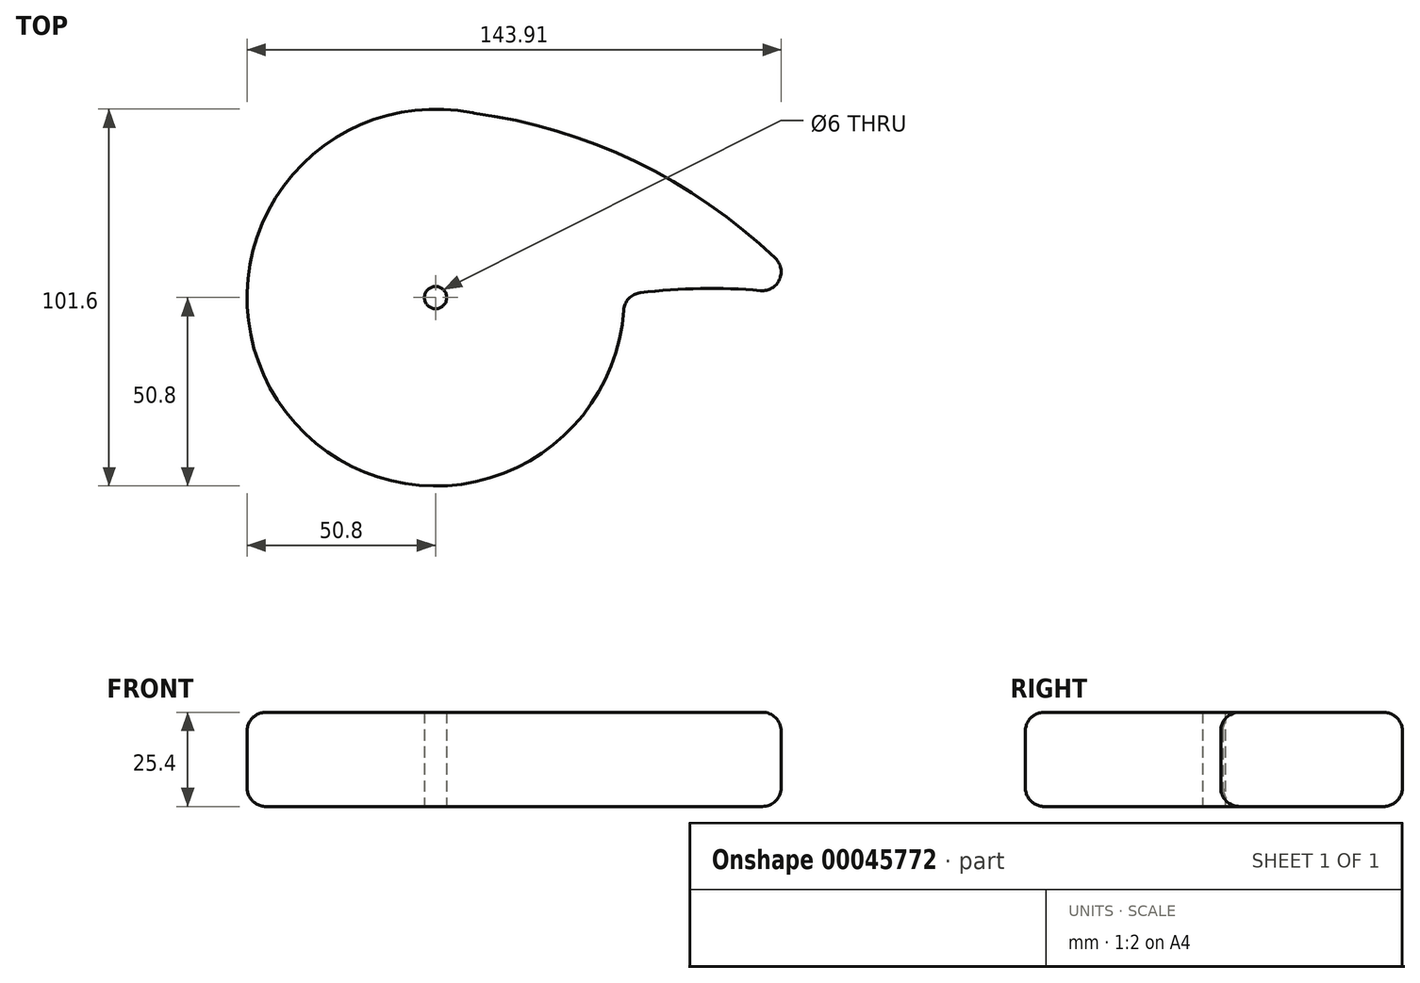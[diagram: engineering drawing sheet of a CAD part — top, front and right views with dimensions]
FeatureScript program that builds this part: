
annotation { "Feature Type Name" : "Feature", "Feature Type Description" : "" }
export const myFeature = defineFeature(function(context is Context, id is Id, definition is map)
    precondition{}
    {
        {
            var Q0;
            Q0=qCreatedBy(makeId("Top.planeOp"),FACE);
            var sketch = newSketch(context, id + "F0", { "sketchPlane" : qUnion([Q0])});
            skPoint(sketch, "E0", {"position": v(0, 50.8) * mm});
            skPoint(sketch, "E1", {"position": v(46.63, 0) * mm});
            skArc(sketch, "E2", {"start": v(10.1, 49.78) * mm, "mid": v(-39.11, -32.42) * mm, "end": v(50.8, 0.7) * mm});
            skPoint(sketch, "E3", {"position": v(0, 3) * mm});
            skCircle(sketch, "E4", {"center": v(0, 0) * mm, "radius": 3 * mm});
            skPoint(sketch, "E5", {"position": v(101.6, 0) * mm});
            skArc(sketch, "E6", {"start": v(101.6, 0) * mm, "mid": v(55.92, 35.65) * mm, "end": v(0, 50.8) * mm});
            skArc(sketch, "E7", {"start": v(101.6, 0) * mm, "mid": v(76.23, 2.45) * mm, "end": v(50.8, 0.7) * mm});
            skSolve(sketch);
        }
        {
            var Q0;
            Q0 = qSketchRegion(id + "F0", true);
            extrude(context, id + "F1", {"entities" : qUnion([Q0]), "depth" : 25.4 * mm});
        }
        {
            var Q0;
            Q0=makeQuery(id+"F1.opExtrude","SWEPT_EDGE",EDGE,{"disambiguationData":[OSD([sQuery(id+"F0.wireOp",EDGE,"E2"),sQuery(id+"F0.wireOp",EDGE,"E7")])]});
            var Q1;
            Q1=makeQuery(id+"F1.opExtrude","SWEPT_EDGE",EDGE,{"disambiguationData":[OSD([sQuery(id+"F0.wireOp",EDGE,"E6"),sQuery(id+"F0.wireOp",EDGE,"E7")])]});
            var Q2;
            Q2=makeQuery(id+"F1.opExtrude","SWEPT_EDGE",EDGE,{"disambiguationData":[OSD([sQuery(id+"F0.wireOp",EDGE,"E2"),sQuery(id+"F0.wireOp",EDGE,"E6")])]});
            fillet(context, id + "F2", {"entities" : qUnion([Q0, Q1, Q2]), "radius" : 5.08 * mm, "tangentPropagation" : true, "allowEdgeOverflow" : false});
        }
        {
            var Q0;
            Q0=makeQuery(id+"F1.opExtrude","CAP_EDGE",EDGE,{"disambiguationData":[OSD([sQuery(id+"F0.wireOp",EDGE,"E2")])],"isStart":false});
            var Q1;
            Q1=makeQuery(id+"F1.opExtrude","CAP_EDGE",EDGE,{"disambiguationData":[OSD([sQuery(id+"F0.wireOp",EDGE,"E2")])],"isStart":true});
            fillet(context, id + "F3", {"entities" : qUnion([Q0, Q1]), "radius" : 5.08 * mm, "tangentPropagation" : true, "allowEdgeOverflow" : false});
        }
    });
